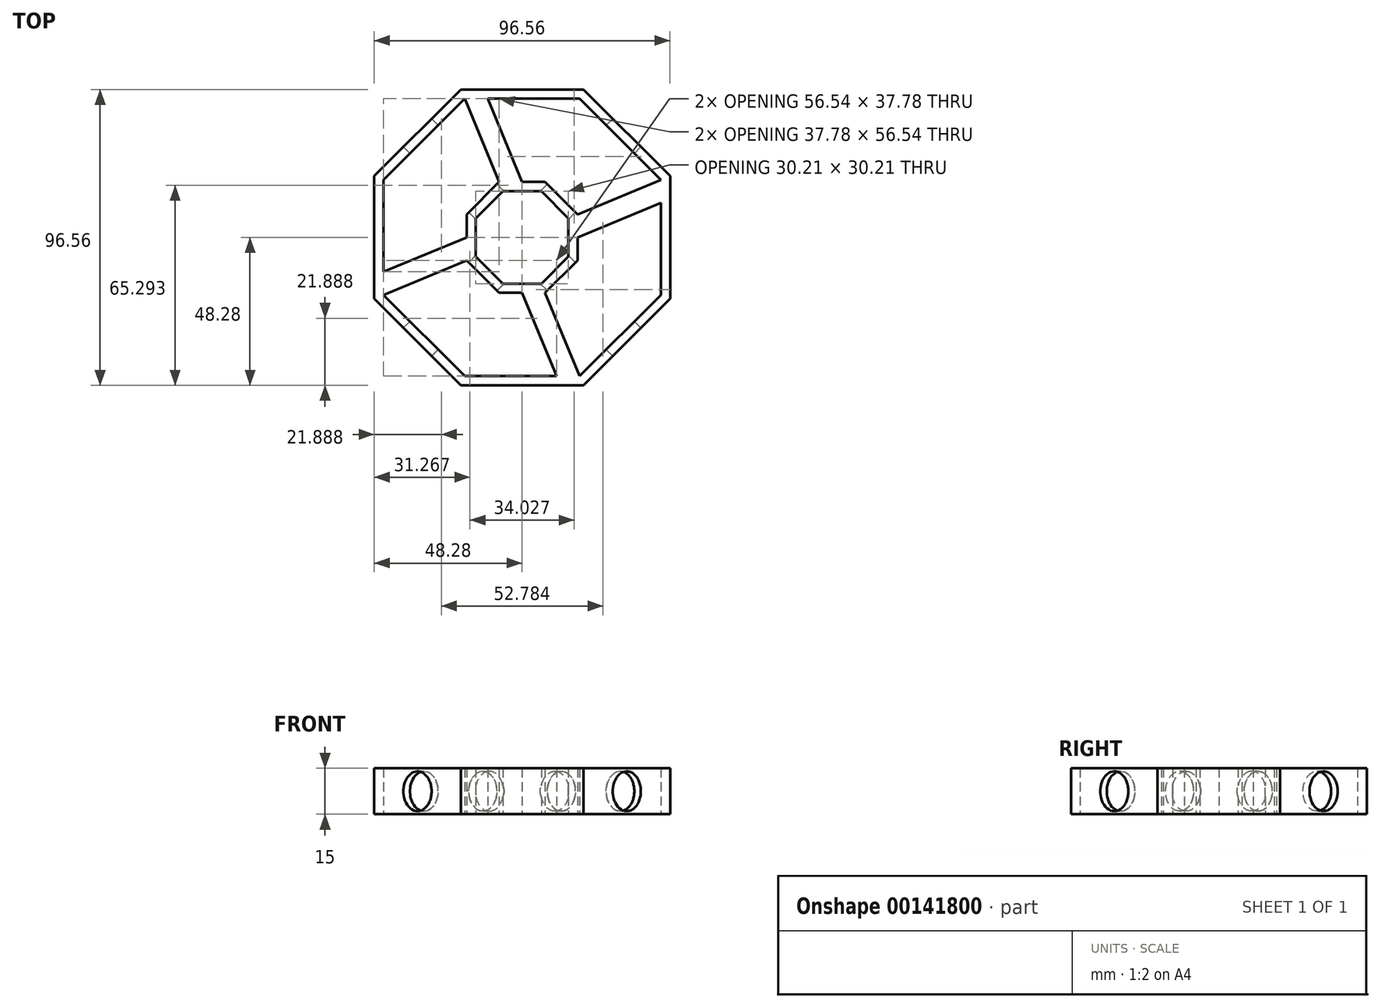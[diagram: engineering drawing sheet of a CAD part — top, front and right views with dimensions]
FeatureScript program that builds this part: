
annotation { "Feature Type Name" : "Feature", "Feature Type Description" : "" }
export const myFeature = defineFeature(function(context is Context, id is Id, definition is map)
    precondition{}
    {
        {
            var Q0;
            Q0=qCreatedBy(makeId("Top.planeOp"),FACE);
            var sketch = newSketch(context, id + "F0", { "sketchPlane" : qUnion([Q0])});
            skCircle(sketch, "E0.cCircle", {"center": v(0, 0) * mm, "radius": 48.28 * mm, "construction": true});
            skLineSegment(sketch, "E0.0", {"start": v(-48.28, -20) * mm, "end": v(-48.28, 20) * mm});
            skLineSegment(sketch, "E0.1", {"start": v(-48.28, 20) * mm, "end": v(-20, 48.28) * mm});
            skLineSegment(sketch, "E0.2", {"start": v(-20, 48.28) * mm, "end": v(20, 48.28) * mm});
            skLineSegment(sketch, "E0.3", {"start": v(20, 48.28) * mm, "end": v(48.28, 20) * mm});
            skLineSegment(sketch, "E0.4", {"start": v(48.28, 20) * mm, "end": v(48.28, -20) * mm});
            skLineSegment(sketch, "E0.5", {"start": v(48.28, -20) * mm, "end": v(20, -48.28) * mm});
            skLineSegment(sketch, "E0.6", {"start": v(20, -48.28) * mm, "end": v(-20, -48.28) * mm});
            skLineSegment(sketch, "E0.7", {"start": v(-20, -48.28) * mm, "end": v(-48.28, -20) * mm});
            skPoint(sketch, "E0.0.midPoint", {"position": v(-48.28, 0) * mm});
            skCircle(sketch, "E1.cCircle", {"center": v(0, 0) * mm, "radius": 45.28 * mm, "construction": true});
            skLineSegment(sketch, "E1.0", {"start": v(-45.28, -18.76) * mm, "end": v(-45.28, 18.76) * mm});
            skLineSegment(sketch, "E1.1", {"start": v(-45.28, 18.76) * mm, "end": v(-18.76, 45.28) * mm});
            skLineSegment(sketch, "E1.2", {"start": v(-18.76, 45.28) * mm, "end": v(18.76, 45.28) * mm});
            skLineSegment(sketch, "E1.3", {"start": v(18.76, 45.28) * mm, "end": v(45.28, 18.76) * mm});
            skLineSegment(sketch, "E1.4", {"start": v(45.28, 18.76) * mm, "end": v(45.28, -18.76) * mm});
            skLineSegment(sketch, "E1.5", {"start": v(45.28, -18.76) * mm, "end": v(18.76, -45.28) * mm});
            skLineSegment(sketch, "E1.6", {"start": v(18.76, -45.28) * mm, "end": v(-18.76, -45.28) * mm});
            skLineSegment(sketch, "E1.7", {"start": v(-18.76, -45.28) * mm, "end": v(-45.28, -18.76) * mm});
            skPoint(sketch, "E1.0.midPoint", {"position": v(-45.28, 0) * mm});
            skCircle(sketch, "E2.cCircle", {"center": v(0, 0) * mm, "radius": 15.1 * mm, "construction": true});
            skLineSegment(sketch, "E2.0", {"start": v(-15.1, -6.26) * mm, "end": v(-15.1, 6.26) * mm});
            skLineSegment(sketch, "E2.1", {"start": v(-15.1, 6.26) * mm, "end": v(-6.26, 15.1) * mm});
            skLineSegment(sketch, "E2.2", {"start": v(-6.26, 15.1) * mm, "end": v(6.26, 15.1) * mm});
            skLineSegment(sketch, "E2.3", {"start": v(6.26, 15.1) * mm, "end": v(15.1, 6.26) * mm});
            skLineSegment(sketch, "E2.4", {"start": v(15.1, 6.26) * mm, "end": v(15.1, -6.26) * mm});
            skLineSegment(sketch, "E2.5", {"start": v(15.1, -6.26) * mm, "end": v(6.26, -15.1) * mm});
            skLineSegment(sketch, "E2.6", {"start": v(6.26, -15.1) * mm, "end": v(-6.26, -15.1) * mm});
            skLineSegment(sketch, "E2.7", {"start": v(-6.26, -15.1) * mm, "end": v(-15.1, -6.26) * mm});
            skPoint(sketch, "E2.0.midPoint", {"position": v(-15.1, 0) * mm});
            skCircle(sketch, "E3.cCircle", {"center": v(0, 0) * mm, "radius": 18.1 * mm, "construction": true});
            skLineSegment(sketch, "E3.0", {"start": v(-18.1, -7.5) * mm, "end": v(-18.1, 7.5) * mm});
            skLineSegment(sketch, "E3.1", {"start": v(-18.1, 7.5) * mm, "end": v(-7.5, 18.1) * mm});
            skLineSegment(sketch, "E3.2", {"start": v(-7.5, 18.1) * mm, "end": v(7.5, 18.1) * mm});
            skLineSegment(sketch, "E3.3", {"start": v(7.5, 18.1) * mm, "end": v(18.1, 7.5) * mm});
            skLineSegment(sketch, "E3.4", {"start": v(18.1, 7.5) * mm, "end": v(18.1, -7.5) * mm});
            skLineSegment(sketch, "E3.5", {"start": v(18.1, -7.5) * mm, "end": v(7.5, -18.1) * mm});
            skLineSegment(sketch, "E3.6", {"start": v(7.5, -18.1) * mm, "end": v(-7.5, -18.1) * mm});
            skLineSegment(sketch, "E3.7", {"start": v(-7.5, -18.1) * mm, "end": v(-18.1, -7.5) * mm});
            skPoint(sketch, "E3.0.midPoint", {"position": v(-18.1, 0) * mm});
            skLineSegment(sketch, "E4", {"start": v(-18.76, 45.28) * mm, "end": v(-7.5, 18.1) * mm});
            skLineSegment(sketch, "E5", {"start": v(45.28, 18.76) * mm, "end": v(18.1, 7.5) * mm});
            skLineSegment(sketch, "E6", {"start": v(7.5, -18.1) * mm, "end": v(18.76, -45.28) * mm});
            skLineSegment(sketch, "E7", {"start": v(-18.1, -7.5) * mm, "end": v(-45.28, -18.76) * mm});
            skLineSegment(sketch, "E8", {"start": v(18.1, 0) * mm, "end": v(45.28, 11.26) * mm});
            skLineSegment(sketch, "E9", {"start": v(18.1, 0) * mm, "end": v(45.28, 0) * mm, "construction": true});
            skLineSegment(sketch, "E10", {"start": v(0, -18.1) * mm, "end": v(11.26, -45.28) * mm});
            skLineSegment(sketch, "E11", {"start": v(-18.1, 0) * mm, "end": v(-45.28, -11.26) * mm});
            skLineSegment(sketch, "E12", {"start": v(0, 18.1) * mm, "end": v(-11.26, 45.28) * mm});
            skSolve(sketch);
        }
        {
            var Q0;
            Q0=makeQuery(id+"F0.imprint","IMPRINT",FACE,{"disambiguationData":[TD([[makeQuery(id+"F0.imprint","IMPRINT",EDGE,{"derivedFrom":sQuery(id+"F0.wireOp",EDGE,"E0.0")}),-1.0]])]});
            var Q1;
            Q1=makeQuery(id+"F0.imprint","IMPRINT",FACE,{"disambiguationData":[TD([[makeQuery(id+"F0.imprint","IMPRINT",EDGE,{"derivedFrom":sQuery(id+"F0.wireOp",EDGE,"E2.0")}),1.0]])]});
            var Q2;
            {var subQ1=sQuery(id+"F0.wireOp",EDGE,"E7");Q2=makeQuery(id+"F0.imprint","IMPRINT",FACE,{"disambiguationData":[TD([[makeQuery(id+"F0.imprint","IMPRINT",EDGE,{"derivedFrom":subQ1}),-1.0]])]});}
            var Q3;
            {var subQ0=sQuery(id+"F0.wireOp",EDGE,"E4");Q3=makeQuery(id+"F0.imprint","IMPRINT",FACE,{"disambiguationData":[TD([[makeQuery(id+"F0.imprint","IMPRINT",EDGE,{"derivedFrom":subQ0}),1.0]])]});}
            var Q4;
            {var subQ1=sQuery(id+"F0.wireOp",EDGE,"E5");Q4=makeQuery(id+"F0.imprint","IMPRINT",FACE,{"disambiguationData":[TD([[makeQuery(id+"F0.imprint","IMPRINT",EDGE,{"derivedFrom":subQ1}),1.0]])]});}
            var Q5;
            {var subQ1=sQuery(id+"F0.wireOp",EDGE,"E6");Q5=makeQuery(id+"F0.imprint","IMPRINT",FACE,{"disambiguationData":[TD([[makeQuery(id+"F0.imprint","IMPRINT",EDGE,{"derivedFrom":subQ1}),-1.0]])]});}
            extrude(context, id + "F1", {"entities" : qUnion([Q0, Q1, Q2, Q3, Q4, Q5]), "depth" : 15 * mm});
        }
        {
            var Q0;
            Q0=makeQuery(id+"F1.opExtrude","SWEPT_FACE",FACE,{"disambiguationData":[OSD([sQuery(id+"F0.wireOp",EDGE,"E0.5")])]});
            var sketch = newSketch(context, id + "F2", { "sketchPlane" : qUnion([Q0])});
            skLineSegment(sketch, "E13", {"start": v(-20, 15) * mm, "end": v(20, 0) * mm, "construction": true});
            skCircle(sketch, "E14", {"center": v(0, 7.5) * mm, "radius": 6.5 * mm});
            skSolve(sketch);
        }
        {
            var Q0;
            Q0=makeQuery(id+"F2.imprint","IMPRINT",FACE,{"disambiguationData":[TD([[makeQuery(id+"F2.imprint","IMPRINT",EDGE,{"derivedFrom":sQuery(id+"F2.wireOp",EDGE,"E14")}),1.0]])]});
            extrude(context, id + "F3", {"entities" : qUnion([Q0]), "operationType" : NewBodyOperationType.REMOVE, "endBound" : BoundingType.THROUGH_ALL, "oppositeDirection" : true, "depth" : 25 * mm});
        }
        {
            var Q0;
            Q0=makeQuery(id+"F1.opExtrude","SWEPT_FACE",FACE,{"disambiguationData":[OSD([sQuery(id+"F0.wireOp",EDGE,"E0.7")])]});
            var sketch = newSketch(context, id + "F4", { "sketchPlane" : qUnion([Q0])});
            skLineSegment(sketch, "E15", {"start": v(-20, 15) * mm, "end": v(20, 0) * mm, "construction": true});
            skCircle(sketch, "E16", {"center": v(0, 7.5) * mm, "radius": 6.5 * mm});
            skSolve(sketch);
        }
        {
            var Q0;
            Q0=qSketchRegion(id+"F4",true);
            extrude(context, id + "F5", {"entities" : qUnion([Q0]), "operationType" : NewBodyOperationType.REMOVE, "endBound" : BoundingType.THROUGH_ALL, "oppositeDirection" : true, "depth" : 25 * mm});
        }
    });
